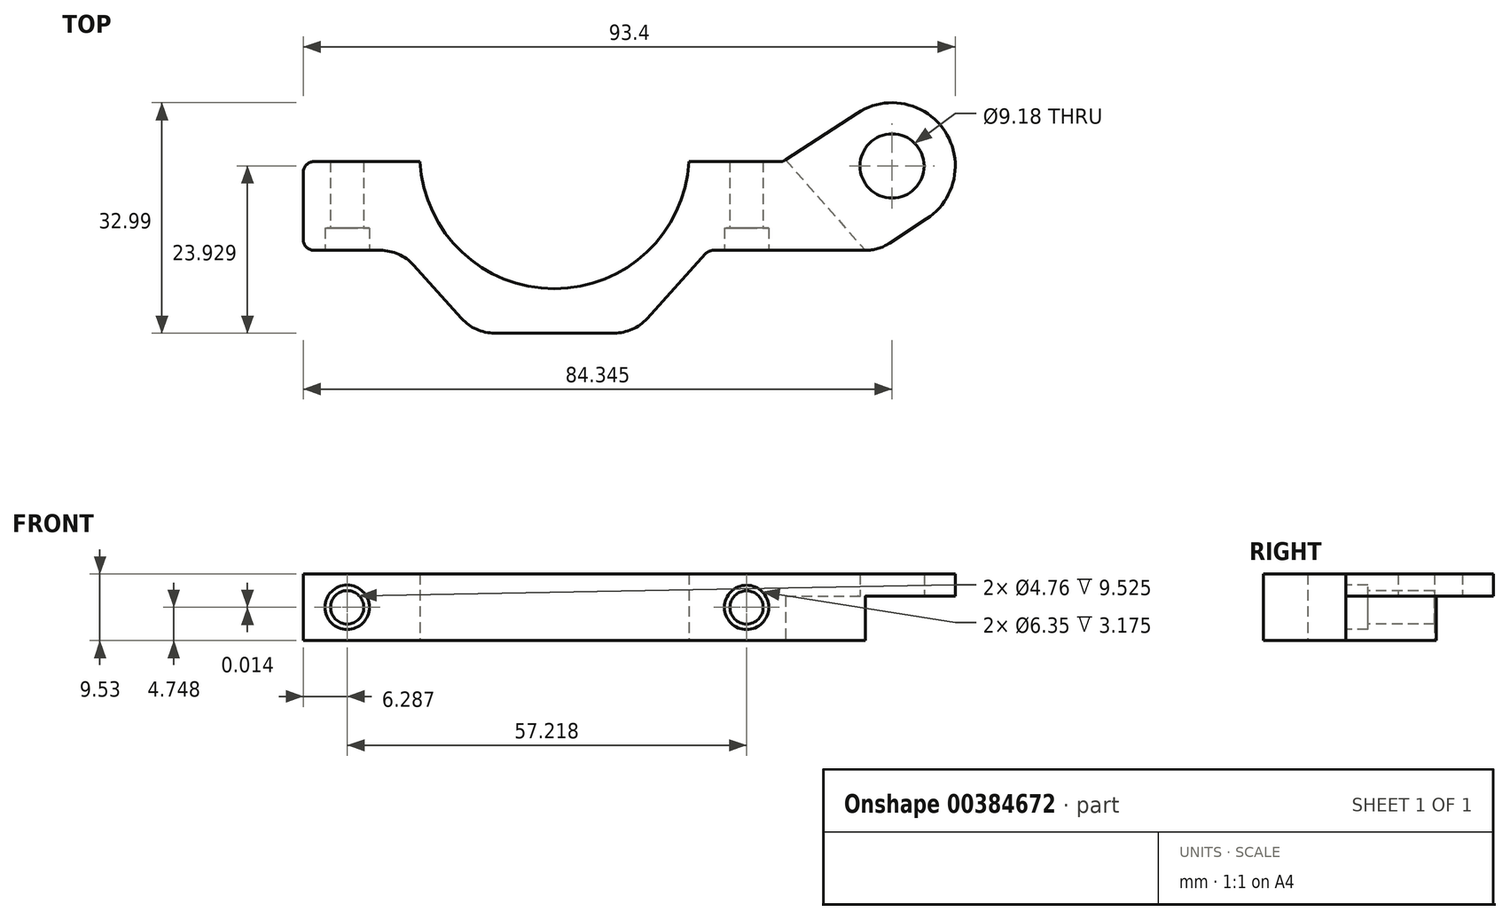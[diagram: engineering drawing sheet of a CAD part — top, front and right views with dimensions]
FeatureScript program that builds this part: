
annotation { "Feature Type Name" : "Feature", "Feature Type Description" : "" }
export const myFeature = defineFeature(function(context is Context, id is Id, definition is map)
    precondition{}
    {
        {
            var Q0;
            Q0=qCreatedBy(makeId("Top.planeOp"),FACE);
            var sketch = newSketch(context, id + "F0", { "sketchPlane" : qUnion([Q0])});
            skCircle(sketch, "E0", {"center": v(31.68, 18.92) * mm, "radius": 4.59 * mm});
            skArc(sketch, "E1", {"start": v(36.63, 11.34) * mm, "mid": v(39.26, 23.87) * mm, "end": v(26.72, 26.5) * mm});
            skLineSegment(sketch, "E2", {"start": v(36.63, 11.34) * mm, "end": v(31.31, 7.87) * mm});
            skLineSegment(sketch, "E3", {"start": v(-8.12, -5.01) * mm, "end": v(-25.28, -5.01) * mm});
            skLineSegment(sketch, "E4", {"start": v(-30, -2.92) * mm, "end": v(-36.9, 4.74) * mm});
            skLineSegment(sketch, "E5", {"start": v(-41.62, 6.83) * mm, "end": v(-51.15, 6.83) * mm});
            skLineSegment(sketch, "E6", {"start": v(-52.67, 8.36) * mm, "end": v(-52.67, 18) * mm});
            skCircle(sketch, "E7", {"center": v(-16.7, 20.64) * mm, "radius": 19.05 * mm, "construction": true});
            skCircle(sketch, "E8.0", {"center": v(-16.7, 20.64) * mm, "radius": 19.3 * mm});
            skLineSegment(sketch, "E9", {"start": v(-51.15, 19.53) * mm, "end": v(-35.97, 19.53) * mm});
            skLineSegment(sketch, "E10", {"start": v(2.57, 19.53) * mm, "end": v(15.6, 19.53) * mm});
            skLineSegment(sketch, "E11", {"start": v(16.43, 19.78) * mm, "end": v(26.72, 26.5) * mm});
            skPoint(sketch, "E12.visualSharp", {"position": v(-38.8, 6.83) * mm});
            skArc(sketch, "E12.filletArc", {"start": v(-36.9, 4.74) * mm, "mid": v(-39.04, 6.29) * mm, "end": v(-41.62, 6.83) * mm});
            skPoint(sketch, "E13.visualSharp", {"position": v(-28.1, -5.01) * mm});
            skArc(sketch, "E13.filletArc", {"start": v(-30, -2.92) * mm, "mid": v(-27.86, -4.47) * mm, "end": v(-25.28, -5.01) * mm});
            skPoint(sketch, "E14.visualSharp", {"position": v(16.05, 19.53) * mm});
            skArc(sketch, "E14.filletArc", {"start": v(15.6, 19.53) * mm, "mid": v(16.03, 19.6) * mm, "end": v(16.43, 19.78) * mm});
            skPoint(sketch, "E15.visualSharp", {"position": v(-52.67, 6.83) * mm});
            skArc(sketch, "E15.filletArc", {"start": v(-52.67, 8.36) * mm, "mid": v(-52.22, 7.28) * mm, "end": v(-51.15, 6.83) * mm});
            skPoint(sketch, "E16.visualSharp", {"position": v(-52.67, 19.53) * mm});
            skArc(sketch, "E16.filletArc", {"start": v(-51.15, 19.53) * mm, "mid": v(-52.22, 19.09) * mm, "end": v(-52.67, 18) * mm});
            skLineSegment(sketch, "E17", {"start": v(-3.4, -2.92) * mm, "end": v(4.94, 6.33) * mm});
            skLineSegment(sketch, "E18", {"start": v(6.07, 6.83) * mm, "end": v(27.84, 6.83) * mm});
            skArc(sketch, "E19.filletArc", {"start": v(-8.12, -5.01) * mm, "mid": v(-5.54, -4.47) * mm, "end": v(-3.4, -2.92) * mm});
            skPoint(sketch, "E20.visualSharp", {"position": v(5.4, 6.83) * mm});
            skArc(sketch, "E20.filletArc", {"start": v(6.07, 6.83) * mm, "mid": v(5.45, 6.7) * mm, "end": v(4.94, 6.33) * mm});
            skArc(sketch, "E21.filletArc", {"start": v(27.84, 6.83) * mm, "mid": v(29.65, 7.1) * mm, "end": v(31.31, 7.87) * mm});
            skLineSegment(sketch, "E22", {"start": v(-16.7, 20.64) * mm, "end": v(-16.7, -20.32) * mm, "construction": true});
            skSolve(sketch);
        }
        {
            var Q0;
            Q0=makeQuery(id+"F0.imprint","IMPRINT",FACE,{"disambiguationData":[TD([[makeQuery(id+"F0.imprint","IMPRINT",EDGE,{"derivedFrom":sQuery(id+"F0.wireOp",EDGE,"E0")}),-1.0]])]});
            extrude(context, id + "F1", {"entities" : qUnion([Q0]), "depth" : 9.52 * mm});
        }
        {
            var Q0;
            Q0=makeQuery(id+"F1.opExtrude","CAP_FACE",FACE,{"disambiguationData":[OSD([sQuery(id+"F0.wireOp",EDGE,"E0"),sQuery(id+"F0.wireOp",EDGE,"E1"),sQuery(id+"F0.wireOp",EDGE,"E2"),sQuery(id+"F0.wireOp",EDGE,"E3"),sQuery(id+"F0.wireOp",EDGE,"E4"),sQuery(id+"F0.wireOp",EDGE,"E5"),sQuery(id+"F0.wireOp",EDGE,"E6"),sQuery(id+"F0.wireOp",EDGE,"E8.0"),sQuery(id+"F0.wireOp",EDGE,"E9"),sQuery(id+"F0.wireOp",EDGE,"E10"),sQuery(id+"F0.wireOp",EDGE,"E11"),sQuery(id+"F0.wireOp",EDGE,"E12.filletArc"),sQuery(id+"F0.wireOp",EDGE,"E13.filletArc"),sQuery(id+"F0.wireOp",EDGE,"E14.filletArc"),sQuery(id+"F0.wireOp",EDGE,"E15.filletArc"),sQuery(id+"F0.wireOp",EDGE,"E16.filletArc"),sQuery(id+"F0.wireOp",EDGE,"E17"),sQuery(id+"F0.wireOp",EDGE,"E18"),sQuery(id+"F0.wireOp",EDGE,"E19.filletArc"),sQuery(id+"F0.wireOp",EDGE,"E20.filletArc"),sQuery(id+"F0.wireOp",EDGE,"E21.filletArc")])],"isStart":true});
            var sketch = newSketch(context, id + "F2", { "sketchPlane" : qUnion([Q0])});
            skArc(sketch, "E23.0.0", {"start": v(-35.97, -19.53) * mm, "mid": v(-16.7, -1.34) * mm, "end": v(2.57, -19.53) * mm});
            skLineSegment(sketch, "E23.0.1", {"start": v(2.57, -19.53) * mm, "end": v(15.6, -19.53) * mm});
            skArc(sketch, "E23.0.2", {"start": v(15.6, -19.53) * mm, "mid": v(16.03, -19.6) * mm, "end": v(16.43, -19.78) * mm});
            skLineSegment(sketch, "E23.0.3", {"start": v(16.43, -19.78) * mm, "end": v(26.72, -26.5) * mm});
            skArc(sketch, "E23.0.4", {"start": v(26.72, -26.5) * mm, "mid": v(39.26, -23.87) * mm, "end": v(36.63, -11.34) * mm});
            skLineSegment(sketch, "E23.0.5", {"start": v(36.63, -11.34) * mm, "end": v(31.31, -7.87) * mm});
            skArc(sketch, "E23.0.6", {"start": v(31.31, -7.87) * mm, "mid": v(29.65, -7.1) * mm, "end": v(27.84, -6.83) * mm});
            skLineSegment(sketch, "E23.0.7", {"start": v(27.84, -6.83) * mm, "end": v(6.07, -6.83) * mm});
            skArc(sketch, "E23.0.8", {"start": v(6.07, -6.83) * mm, "mid": v(5.45, -6.7) * mm, "end": v(4.94, -6.33) * mm});
            skLineSegment(sketch, "E23.0.9", {"start": v(4.94, -6.33) * mm, "end": v(-3.4, 2.92) * mm});
            skArc(sketch, "E23.0.10", {"start": v(-3.4, 2.92) * mm, "mid": v(-5.54, 4.47) * mm, "end": v(-8.12, 5.01) * mm});
            skLineSegment(sketch, "E23.0.11", {"start": v(-8.12, 5.01) * mm, "end": v(-25.28, 5.01) * mm});
            skArc(sketch, "E23.0.12", {"start": v(-25.28, 5.01) * mm, "mid": v(-27.86, 4.47) * mm, "end": v(-30, 2.92) * mm});
            skLineSegment(sketch, "E23.0.13", {"start": v(-30, 2.92) * mm, "end": v(-36.9, -4.74) * mm});
            skArc(sketch, "E23.0.14", {"start": v(-36.9, -4.74) * mm, "mid": v(-39.04, -6.29) * mm, "end": v(-41.62, -6.83) * mm});
            skLineSegment(sketch, "E23.0.15", {"start": v(-41.62, -6.83) * mm, "end": v(-51.15, -6.83) * mm});
            skArc(sketch, "E23.0.16", {"start": v(-51.15, -6.83) * mm, "mid": v(-52.22, -7.28) * mm, "end": v(-52.67, -8.36) * mm});
            skLineSegment(sketch, "E23.0.17", {"start": v(-52.67, -8.36) * mm, "end": v(-52.67, -18) * mm});
            skArc(sketch, "E23.0.18", {"start": v(-52.67, -18) * mm, "mid": v(-52.22, -19.09) * mm, "end": v(-51.15, -19.53) * mm});
            skLineSegment(sketch, "E23.0.19", {"start": v(-51.15, -19.53) * mm, "end": v(-35.97, -19.53) * mm});
            skLineSegment(sketch, "E24", {"start": v(16.43, -19.78) * mm, "end": v(27.84, -6.83) * mm});
            skSolve(sketch);
        }
        {
            var Q0;
            Q0=makeQuery(id+"F2.imprint","IMPRINT",FACE,{"disambiguationData":[TD([[makeQuery(id+"F2.imprint","IMPRINT",EDGE,{"derivedFrom":sQuery(id+"F2.wireOp",EDGE,"E23.0.3")}),1.0]])]});
            extrude(context, id + "F3", {"entities" : qUnion([Q0]), "operationType" : NewBodyOperationType.REMOVE, "oppositeDirection" : true, "depth" : 6.35 * mm});
        }
        {
            var Q0;
            Q0=makeQuery(id+"F1.opExtrude","SWEPT_FACE",FACE,{"disambiguationData":[OSD([sQuery(id+"F0.wireOp",EDGE,"E18")])]});
            var sketch = newSketch(context, id + "F4", { "sketchPlane" : qUnion([Q0])});
            skLineSegment(sketch, "E25.0.0", {"start": v(-51.15, 0) * mm, "end": v(-41.62, 0) * mm});
            skLineSegment(sketch, "E25.0.1", {"start": v(-41.62, 0) * mm, "end": v(-41.62, 9.53) * mm});
            skLineSegment(sketch, "E25.0.2", {"start": v(-41.62, 9.53) * mm, "end": v(-51.15, 9.53) * mm});
            skLineSegment(sketch, "E25.0.3", {"start": v(-51.15, 9.53) * mm, "end": v(-51.15, 0) * mm});
            skLineSegment(sketch, "E26.0.0", {"start": v(6.07, 0) * mm, "end": v(27.84, 0) * mm});
            skLineSegment(sketch, "E26.0.1", {"start": v(27.84, 0) * mm, "end": v(27.84, 6.35) * mm});
            skLineSegment(sketch, "E26.0.2", {"start": v(27.84, 6.35) * mm, "end": v(27.84, 9.53) * mm});
            skLineSegment(sketch, "E26.0.3", {"start": v(27.84, 9.53) * mm, "end": v(6.07, 9.53) * mm});
            skLineSegment(sketch, "E26.0.4", {"start": v(6.07, 9.53) * mm, "end": v(6.07, 0) * mm});
            skLineSegment(sketch, "E27.0", {"start": v(15.6, 9.53) * mm, "end": v(15.6, 0) * mm});
            skPoint(sketch, "E28", {"position": v(-46.38, 4.76) * mm});
            skPoint(sketch, "E28.positionSnap0", {"position": v(-41.62, 4.76) * mm});
            skPoint(sketch, "E29", {"position": v(10.84, 4.75) * mm});
            skSolve(sketch);
        }
        {
            var Q0;
            Q0=sQuery(id+"F4.wireOp",VERTEX,"E28");
            var Q1;
            Q1=sQuery(id+"F4.wireOp",VERTEX,"E29");
            var Q2;
            Q2=makeQuery(id+"F1.opExtrude","SWEPT_BODY",BODY,{"disambiguationData":[OSD([sQuery(id+"F0.wireOp",EDGE,"E0"),sQuery(id+"F0.wireOp",EDGE,"E1"),sQuery(id+"F0.wireOp",EDGE,"E2"),sQuery(id+"F0.wireOp",EDGE,"E3"),sQuery(id+"F0.wireOp",EDGE,"E4"),sQuery(id+"F0.wireOp",EDGE,"E5"),sQuery(id+"F0.wireOp",EDGE,"E6"),sQuery(id+"F0.wireOp",EDGE,"E8.0"),sQuery(id+"F0.wireOp",EDGE,"E9"),sQuery(id+"F0.wireOp",EDGE,"E10"),sQuery(id+"F0.wireOp",EDGE,"E11"),sQuery(id+"F0.wireOp",EDGE,"E12.filletArc"),sQuery(id+"F0.wireOp",EDGE,"E13.filletArc"),sQuery(id+"F0.wireOp",EDGE,"E14.filletArc"),sQuery(id+"F0.wireOp",EDGE,"E15.filletArc"),sQuery(id+"F0.wireOp",EDGE,"E16.filletArc"),sQuery(id+"F0.wireOp",EDGE,"E17"),sQuery(id+"F0.wireOp",EDGE,"E18"),sQuery(id+"F0.wireOp",EDGE,"E19.filletArc"),sQuery(id+"F0.wireOp",EDGE,"E20.filletArc"),sQuery(id+"F0.wireOp",EDGE,"E21.filletArc")])]});
            hole(context, id + "F5", {"style" : HoleStyle.C_BORE, "endStyle" : HoleEndStyle.BLIND, "holeDiameter" : 4.76 * mm, "cBoreDiameter" : 6.35 * mm, "cBoreDepth" : 3.17 * mm, "holeDepth" : 12.7 * mm, "isTappedThrough" : true, "tappedDepth" : 12.7 * mm, "tapClearance" : 3, "locations" : qUnion([Q0, Q1]), "scope" : qUnion([Q2])});
        }
    });
